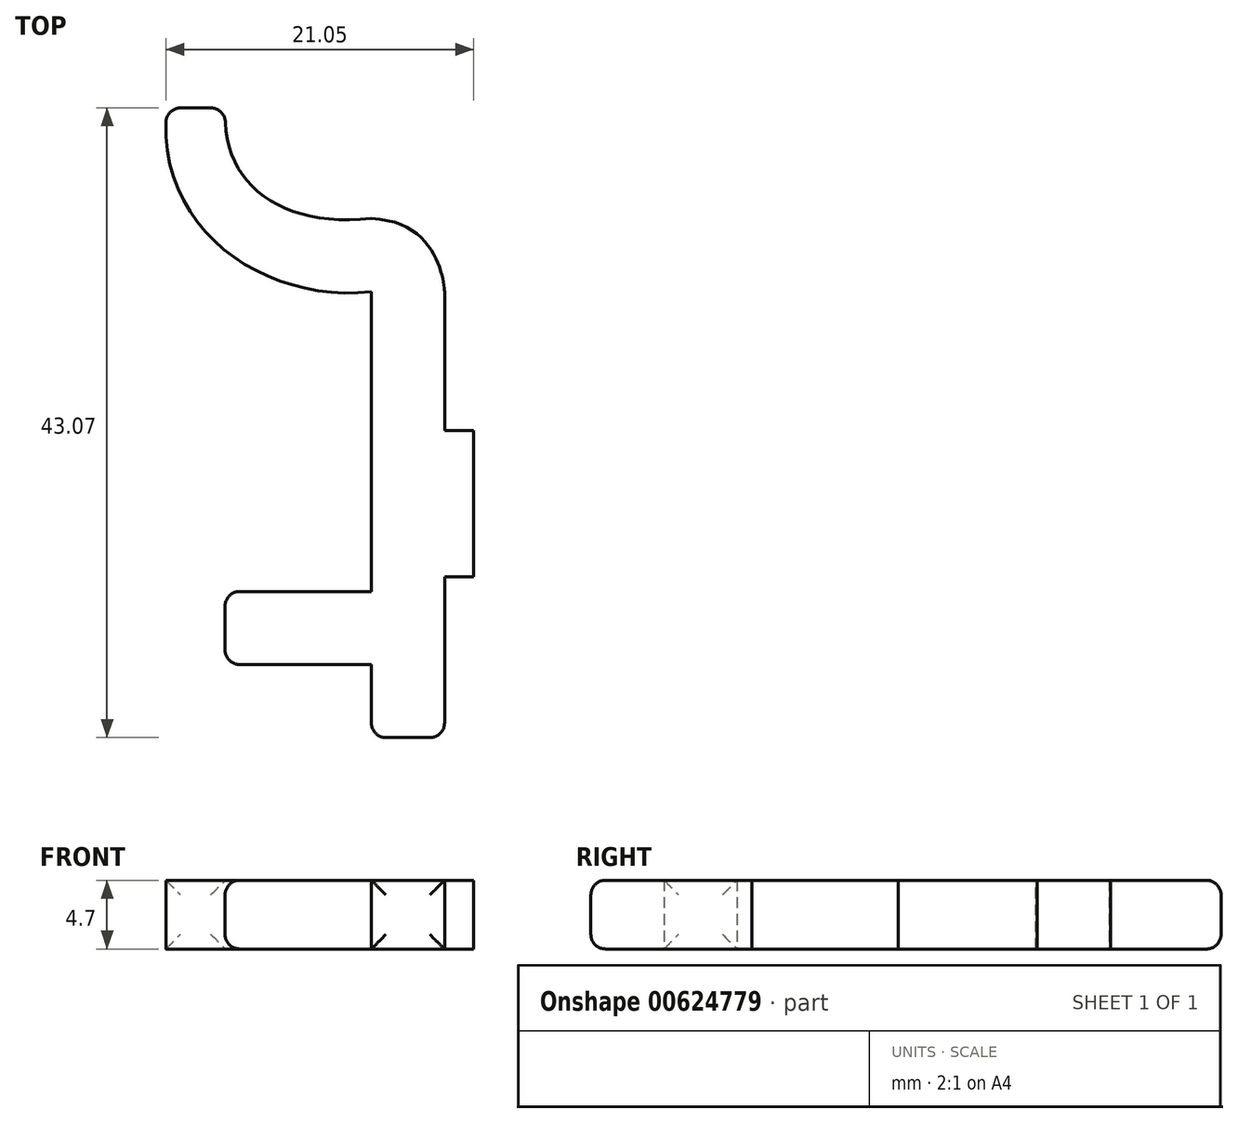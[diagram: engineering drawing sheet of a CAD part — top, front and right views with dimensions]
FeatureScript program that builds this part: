
annotation { "Feature Type Name" : "Feature", "Feature Type Description" : "" }
export const myFeature = defineFeature(function(context is Context, id is Id, definition is map)
    precondition{}
    {
        {
            var Q0;
            Q0=qCreatedBy(makeId("Top.planeOp"),FACE);
            var sketch = newSketch(context, id + "F0", { "sketchPlane" : qUnion([Q0])});
            skLineSegment(sketch, "E0", {"start": v(-13.96, 33.07) * mm, "end": v(-9.96, 33.07) * mm});
            skFitSpline(sketch, "E1", {"points": [v(-9.96, 33.07) * mm, v(0, 25.5) * mm], "startDerivative": vector(-1.06, -15.17) * mm, "endDerivative": vector(19.05, 1.96) * mm});
            skFitSpline(sketch, "E2", {"points": [v(0, 25.5) * mm, v(5, 20.5) * mm], "startDerivative": vector(13.6, -0.54) * mm, "endDerivative": vector(0.17, -2.2) * mm});
            skFitSpline(sketch, "E3", {"points": [v(-13.96, 33.07) * mm, v(0, 20.5) * mm], "startDerivative": vector(-2.9, -24.56) * mm, "endDerivative": vector(21.9, 2.52) * mm});
            skLineSegment(sketch, "E4", {"start": v(5, 20.5) * mm, "end": v(5, -10) * mm});
            skLineSegment(sketch, "E5", {"start": v(5, -10) * mm, "end": v(0, -10) * mm});
            skLineSegment(sketch, "E6", {"start": v(0, -10) * mm, "end": v(0, -5) * mm});
            skLineSegment(sketch, "E7", {"start": v(0, -5) * mm, "end": v(-10, -5) * mm});
            skLineSegment(sketch, "E8", {"start": v(-10, -5) * mm, "end": v(-10, 0) * mm});
            skLineSegment(sketch, "E9", {"start": v(-10, 0) * mm, "end": v(0, 0) * mm});
            skLineSegment(sketch, "E10", {"start": v(0, 0) * mm, "end": v(0, 20.5) * mm});
            skLineSegment(sketch, "E11", {"start": v(5, 1) * mm, "end": v(7, 1) * mm});
            skLineSegment(sketch, "E12", {"start": v(7, 1) * mm, "end": v(7, 11) * mm});
            skLineSegment(sketch, "E13", {"start": v(7, 11) * mm, "end": v(5, 11) * mm});
            skSolve(sketch);
        }
        {
            var Q0;
            Q0 = qSketchRegion(id + "F0", true);
            extrude(context, id + "F1", {"entities" : qUnion([Q0]), "depth" : 4.7 * mm, "offsetDistance" : 25 * mm});
        }
        {
            var Q0;
            Q0=makeQuery(id+"F1.opExtrude","SWEPT_FACE",FACE,{"disambiguationData":[OSD([sQuery(id+"F0.wireOp",EDGE,"E0")])]});
            fillet(context, id + "F2", {"entities" : qUnion([Q0]), "radius" : 1 * mm, "tangentPropagation" : true, "allowEdgeOverflow" : false});
        }
        {
            var Q0;
            Q0=makeQuery(id+"F1.opExtrude","SWEPT_FACE",FACE,{"disambiguationData":[OSD([sQuery(id+"F0.wireOp",EDGE,"E8")])]});
            fillet(context, id + "F3", {"entities" : qUnion([Q0]), "radius" : 1 * mm, "tangentPropagation" : true, "allowEdgeOverflow" : false});
        }
        {
            var Q0;
            Q0=makeQuery(id+"F1.opExtrude","SWEPT_FACE",FACE,{"disambiguationData":[OSD([sQuery(id+"F0.wireOp",EDGE,"E5")])]});
            fillet(context, id + "F4", {"entities" : qUnion([Q0]), "radius" : 1 * mm, "tangentPropagation" : true, "allowEdgeOverflow" : false});
        }
    });
